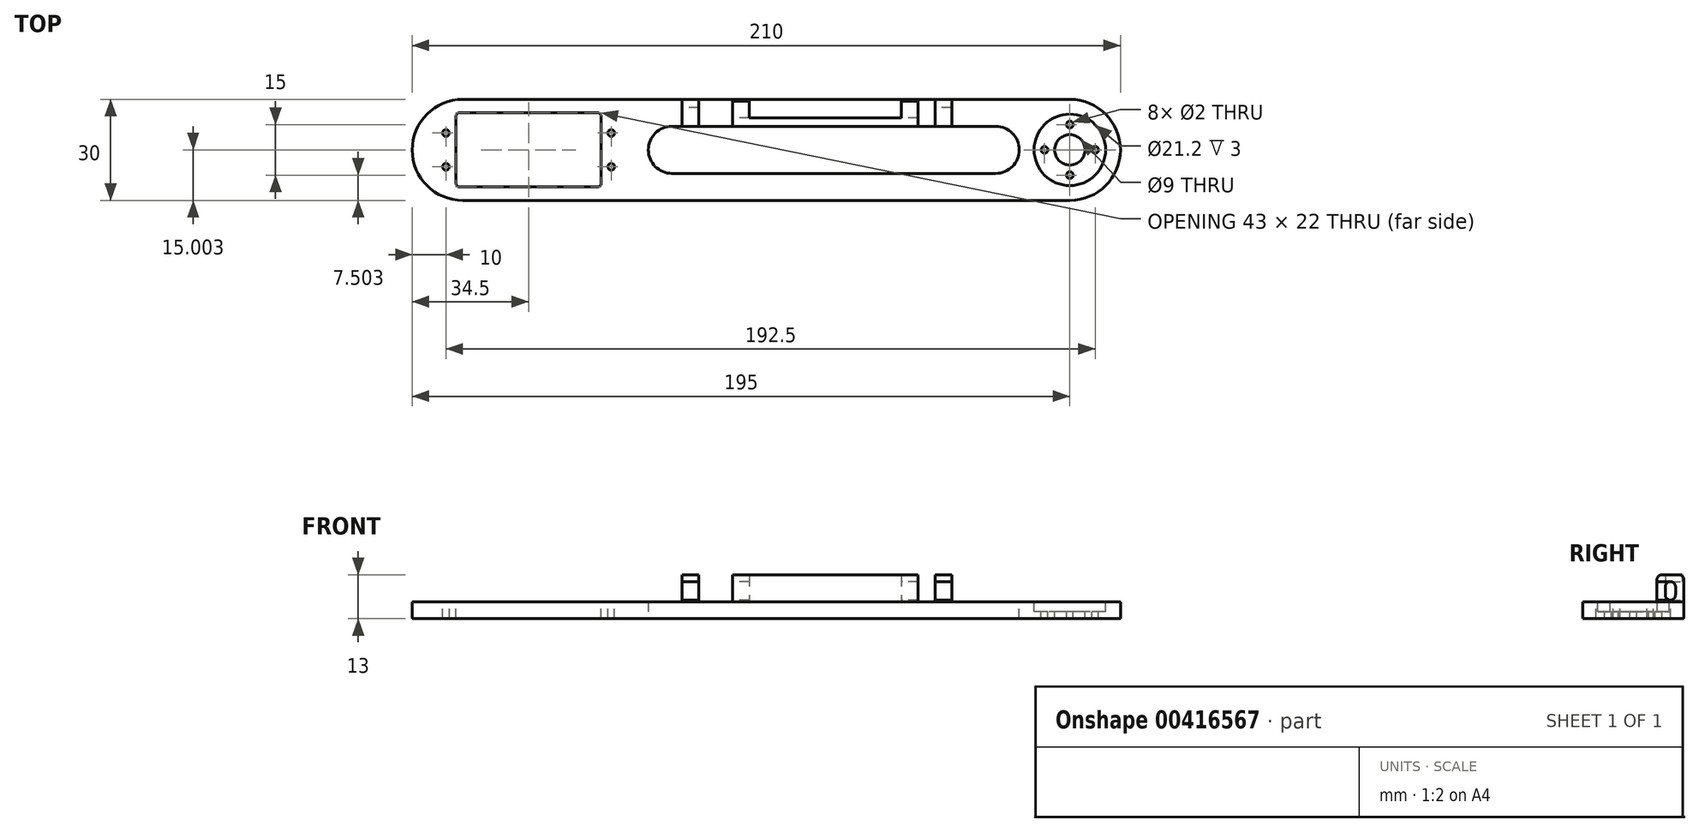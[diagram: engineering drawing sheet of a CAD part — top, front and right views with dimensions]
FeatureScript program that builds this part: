
annotation { "Feature Type Name" : "Feature", "Feature Type Description" : "" }
export const myFeature = defineFeature(function(context is Context, id is Id, definition is map)
    precondition{}
    {
        {
            var Q0;
            Q0=qCreatedBy(makeId("Top.planeOp"),FACE);
            var sketch = newSketch(context, id + "F0", { "sketchPlane" : qUnion([Q0])});
            skLineSegment(sketch, "E0.bottom", {"start": v(-110, 3.1) * mm, "end": v(100, 3.1) * mm});
            skLineSegment(sketch, "E0.top", {"start": v(-110, -26.9) * mm, "end": v(100, -26.9) * mm});
            skLineSegment(sketch, "E0.left", {"start": v(-110, 3.1) * mm, "end": v(-110, -26.9) * mm});
            skLineSegment(sketch, "E0.right", {"start": v(100, 3.1) * mm, "end": v(100, -26.9) * mm});
            skLineSegment(sketch, "E1.bottom", {"start": v(-40, -4.9) * mm, "end": v(70, -4.9) * mm});
            skLineSegment(sketch, "E1.top", {"start": v(-40, -18.9) * mm, "end": v(70, -18.9) * mm});
            skLineSegment(sketch, "E1.left", {"start": v(-40, -4.9) * mm, "end": v(-40, -18.9) * mm});
            skLineSegment(sketch, "E1.right", {"start": v(70, -4.9) * mm, "end": v(70, -18.9) * mm});
            skSolve(sketch);
        }
        {
            var Q0;
            Q0=makeQuery(id+"F0.imprint","IMPRINT",FACE,{"disambiguationData":[TD([[makeQuery(id+"F0.imprint","IMPRINT",EDGE,{"derivedFrom":sQuery(id+"F0.wireOp",EDGE,"E0.bottom")}),-1.0]])]});
            extrude(context, id + "F1", {"entities" : qUnion([Q0]), "depth" : 5 * mm});
        }
        {
            var Q0;
            Q0=makeQuery(id+"F1.opExtrude","CAP_FACE",FACE,{"disambiguationData":[OSD([sQuery(id+"F0.wireOp",EDGE,"E0.bottom"),sQuery(id+"F0.wireOp",EDGE,"E0.top"),sQuery(id+"F0.wireOp",EDGE,"E0.left"),sQuery(id+"F0.wireOp",EDGE,"E0.right")])],"isStart":false});
            var sketch = newSketch(context, id + "F2", { "sketchPlane" : qUnion([Q0])});
            skCircle(sketch, "E2", {"center": v(85, -11.9) * mm, "radius": 10.6 * mm});
            skCircle(sketch, "E3", {"center": v(85, -11.9) * mm, "radius": 4.5 * mm});
            skCircle(sketch, "E4", {"center": v(85, -4.4) * mm, "radius": 1 * mm});
            skCircle(sketch, "E5", {"center": v(85, -19.4) * mm, "radius": 1 * mm});
            skCircle(sketch, "E6", {"center": v(92.5, -11.9) * mm, "radius": 1 * mm});
            skCircle(sketch, "E7", {"center": v(77.5, -11.9) * mm, "radius": 1 * mm});
            skCircle(sketch, "E8", {"center": v(-65, -11.9) * mm, "radius": 2.75 * mm});
            skLineSegment(sketch, "E9.bottom", {"start": v(-97, -0.9) * mm, "end": v(-54, -0.9) * mm});
            skLineSegment(sketch, "E9.top", {"start": v(-97, -22.9) * mm, "end": v(-54, -22.9) * mm});
            skLineSegment(sketch, "E9.left", {"start": v(-97, -0.9) * mm, "end": v(-97, -22.9) * mm});
            skLineSegment(sketch, "E9.right", {"start": v(-54, -0.9) * mm, "end": v(-54, -22.9) * mm});
            skCircle(sketch, "E10", {"center": v(-51, -6.9) * mm, "radius": 1 * mm});
            skCircle(sketch, "E11", {"center": v(-51, -16.9) * mm, "radius": 1 * mm});
            skCircle(sketch, "E12", {"center": v(-100, -6.9) * mm, "radius": 1 * mm});
            skCircle(sketch, "E13", {"center": v(-100, -16.9) * mm, "radius": 1 * mm});
            skSolve(sketch);
        }
        {
            var Q0;
            Q0=makeQuery(id+"F2.imprint","IMPRINT",FACE,{"disambiguationData":[TD([[makeQuery(id+"F2.imprint","IMPRINT",EDGE,{"derivedFrom":sQuery(id+"F2.wireOp",EDGE,"E2")}),1.0]])]});
            var Q1;
            Q1=makeQuery(id+"F2.imprint","IMPRINT",FACE,{"disambiguationData":[TD([[makeQuery(id+"F2.imprint","IMPRINT",EDGE,{"derivedFrom":sQuery(id+"F2.wireOp",EDGE,"E8")}),-1.0]])]});
            extrude(context, id + "F3", {"entities" : qUnion([Q0, Q1]), "operationType" : NewBodyOperationType.REMOVE, "oppositeDirection" : true, "depth" : 3 * mm});
        }
        {
            var Q0;
            Q0=makeQuery(id+"F2.imprint","IMPRINT",FACE,{"disambiguationData":[TD([[makeQuery(id+"F2.imprint","IMPRINT",EDGE,{"derivedFrom":sQuery(id+"F2.wireOp",EDGE,"E3")}),1.0]])]});
            var Q1;
            Q1=makeQuery(id+"F2.imprint","IMPRINT",FACE,{"disambiguationData":[TD([[makeQuery(id+"F2.imprint","IMPRINT",EDGE,{"derivedFrom":sQuery(id+"F2.wireOp",EDGE,"E4")}),1.0]])]});
            var Q2;
            Q2=makeQuery(id+"F2.imprint","IMPRINT",FACE,{"disambiguationData":[TD([[makeQuery(id+"F2.imprint","IMPRINT",EDGE,{"derivedFrom":sQuery(id+"F2.wireOp",EDGE,"E7")}),1.0]])]});
            var Q3;
            Q3=makeQuery(id+"F2.imprint","IMPRINT",FACE,{"disambiguationData":[TD([[makeQuery(id+"F2.imprint","IMPRINT",EDGE,{"derivedFrom":sQuery(id+"F2.wireOp",EDGE,"E5")}),1.0]])]});
            var Q4;
            Q4=makeQuery(id+"F2.imprint","IMPRINT",FACE,{"disambiguationData":[TD([[makeQuery(id+"F2.imprint","IMPRINT",EDGE,{"derivedFrom":sQuery(id+"F2.wireOp",EDGE,"E6")}),1.0]])]});
            var Q5;
            Q5=makeQuery(id+"F2.imprint","IMPRINT",FACE,{"disambiguationData":[TD([[makeQuery(id+"F2.imprint","IMPRINT",EDGE,{"derivedFrom":sQuery(id+"F2.wireOp",EDGE,"E8")}),1.0]])]});
            var Q6;
            Q6=makeQuery(id+"F2.imprint","IMPRINT",FACE,{"disambiguationData":[TD([[makeQuery(id+"F2.imprint","IMPRINT",EDGE,{"derivedFrom":sQuery(id+"F2.wireOp",EDGE,"BxBnCqye-svmn-VfxW-Yds5-lMc6FiJJZGoG")}),1.0]])]});
            var Q7;
            Q7=makeQuery(id+"F2.imprint","IMPRINT",FACE,{"disambiguationData":[TD([[makeQuery(id+"F2.imprint","IMPRINT",EDGE,{"derivedFrom":sQuery(id+"F2.wireOp",EDGE,"Fvn0a9T8-UYAr-KfxW-xJAN-rbL94ZbWyBAD")}),1.0]])]});
            var Q8;
            Q8=makeQuery(id+"F2.imprint","IMPRINT",FACE,{"disambiguationData":[TD([[makeQuery(id+"F2.imprint","IMPRINT",EDGE,{"derivedFrom":sQuery(id+"F2.wireOp",EDGE,"IbQh5voC-LfIl-WeLM-aWEU-xkcyqfmnFLrg")}),1.0]])]});
            var Q9;
            Q9=makeQuery(id+"F2.imprint","IMPRINT",FACE,{"disambiguationData":[TD([[makeQuery(id+"F2.imprint","IMPRINT",EDGE,{"derivedFrom":sQuery(id+"F2.wireOp",EDGE,"Jml5Gy1f-vHH9-9BCY-gYTi-q249JlMg9aTh")}),1.0]])]});
            var Q10;
            Q10=makeQuery(id+"F2.imprint","IMPRINT",FACE,{"disambiguationData":[TD([[makeQuery(id+"F2.imprint","IMPRINT",EDGE,{"derivedFrom":sQuery(id+"F2.wireOp",EDGE,"E8")}),-1.0]])]});
            var Q11;
            Q11=makeQuery(id+"F2.imprint","IMPRINT",FACE,{"disambiguationData":[TD([[makeQuery(id+"F2.imprint","IMPRINT",EDGE,{"derivedFrom":sQuery(id+"F2.wireOp",EDGE,"PWfKf39f-ZtnN-yRcJ-nhmC-XpGRIvCBta7a")}),1.0]])]});
            var Q12;
            Q12=makeQuery(id+"F2.imprint","IMPRINT",FACE,{"disambiguationData":[TD([[makeQuery(id+"F2.imprint","IMPRINT",EDGE,{"derivedFrom":sQuery(id+"F2.wireOp",EDGE,"gZUGkUCZ-vtm3-Om3j-GvZn-Frgqdlfowhft")}),1.0]])]});
            extrude(context, id + "F4", {"entities" : qUnion([Q0, Q1, Q2, Q3, Q4, Q5, Q6, Q7, Q8, Q9, Q10, Q11, Q12]), "operationType" : NewBodyOperationType.REMOVE, "oppositeDirection" : true, "depth" : 25 * mm});
        }
        {
            var Q0;
            Q0=makeQuery(id+"F1.opExtrude","SWEPT_EDGE",EDGE,{"disambiguationData":[OSD([sQuery(id+"F0.wireOp",EDGE,"E0.bottom"),sQuery(id+"F0.wireOp",EDGE,"E0.right")])]});
            var Q1;
            Q1=makeQuery(id+"F1.opExtrude","SWEPT_EDGE",EDGE,{"disambiguationData":[OSD([sQuery(id+"F0.wireOp",EDGE,"E0.top"),sQuery(id+"F0.wireOp",EDGE,"E0.right")])]});
            var Q2;
            Q2=makeQuery(id+"F1.opExtrude","SWEPT_EDGE",EDGE,{"disambiguationData":[OSD([sQuery(id+"F0.wireOp",EDGE,"E0.top"),sQuery(id+"F0.wireOp",EDGE,"E0.left")])]});
            var Q3;
            Q3=makeQuery(id+"F1.opExtrude","SWEPT_EDGE",EDGE,{"disambiguationData":[OSD([sQuery(id+"F0.wireOp",EDGE,"E0.bottom"),sQuery(id+"F0.wireOp",EDGE,"E0.left")])]});
            fillet(context, id + "F5", {"entities" : qUnion([Q0, Q1, Q2, Q3]), "radius" : 15 * mm, "tangentPropagation" : true, "allowEdgeOverflow" : false});
        }
        {
            var Q0;
            Q0=makeQuery(id+"F1.opExtrude","SWEPT_EDGE",EDGE,{"disambiguationData":[OSD([sQuery(id+"F0.wireOp",EDGE,"E1.bottom"),sQuery(id+"F0.wireOp",EDGE,"E1.left")])]});
            var Q1;
            Q1=makeQuery(id+"F1.opExtrude","SWEPT_EDGE",EDGE,{"disambiguationData":[OSD([sQuery(id+"F0.wireOp",EDGE,"E1.top"),sQuery(id+"F0.wireOp",EDGE,"E1.left")])]});
            var Q2;
            Q2=makeQuery(id+"F1.opExtrude","SWEPT_EDGE",EDGE,{"disambiguationData":[OSD([sQuery(id+"F0.wireOp",EDGE,"E1.bottom"),sQuery(id+"F0.wireOp",EDGE,"E1.right")])]});
            var Q3;
            Q3=makeQuery(id+"F1.opExtrude","SWEPT_EDGE",EDGE,{"disambiguationData":[OSD([sQuery(id+"F0.wireOp",EDGE,"E1.top"),sQuery(id+"F0.wireOp",EDGE,"E1.right")])]});
            fillet(context, id + "F6", {"entities" : qUnion([Q0, Q1, Q2, Q3]), "radius" : 7 * mm, "tangentPropagation" : true, "allowEdgeOverflow" : false});
        }
        {
            var Q0;
            {var subQ0=sQuery(id+"F2.wireOp",EDGE,"E9.left");var subQ1=sQuery(id+"F2.wireOp",EDGE,"E9.bottom");Q0=makeQuery(id+"F4.boolean.opBoolean","MERGE",EDGE,{"derivedFrom":[makeQuery(id+"F3.boolean.opBoolean","COPY",EDGE,{"derivedFrom":makeQuery(id+"F3.opExtrude","SWEPT_EDGE",EDGE,{"disambiguationData":[OSD([subQ1,subQ0])]})}),makeQuery(id+"F4.opExtrude","SWEPT_EDGE",EDGE,{"disambiguationData":[OSD([subQ1,subQ0])]})]});}
            var Q1;
            {var subQ0=sQuery(id+"F2.wireOp",EDGE,"E9.left");var subQ1=sQuery(id+"F2.wireOp",EDGE,"E9.top");Q1=makeQuery(id+"F4.boolean.opBoolean","MERGE",EDGE,{"derivedFrom":[makeQuery(id+"F3.boolean.opBoolean","COPY",EDGE,{"derivedFrom":makeQuery(id+"F3.opExtrude","SWEPT_EDGE",EDGE,{"disambiguationData":[OSD([subQ1,subQ0])]})}),makeQuery(id+"F4.opExtrude","SWEPT_EDGE",EDGE,{"disambiguationData":[OSD([subQ1,subQ0])]})]});}
            var Q2;
            {var subQ0=sQuery(id+"F2.wireOp",EDGE,"E9.right");var subQ1=sQuery(id+"F2.wireOp",EDGE,"E9.bottom");Q2=makeQuery(id+"F4.boolean.opBoolean","MERGE",EDGE,{"derivedFrom":[makeQuery(id+"F3.boolean.opBoolean","COPY",EDGE,{"derivedFrom":makeQuery(id+"F3.opExtrude","SWEPT_EDGE",EDGE,{"disambiguationData":[OSD([subQ1,subQ0])]})}),makeQuery(id+"F4.opExtrude","SWEPT_EDGE",EDGE,{"disambiguationData":[OSD([subQ1,subQ0])]})]});}
            var Q3;
            {var subQ0=sQuery(id+"F2.wireOp",EDGE,"E9.right");var subQ1=sQuery(id+"F2.wireOp",EDGE,"E9.top");Q3=makeQuery(id+"F4.boolean.opBoolean","MERGE",EDGE,{"derivedFrom":[makeQuery(id+"F3.boolean.opBoolean","COPY",EDGE,{"derivedFrom":makeQuery(id+"F3.opExtrude","SWEPT_EDGE",EDGE,{"disambiguationData":[OSD([subQ1,subQ0])]})}),makeQuery(id+"F4.opExtrude","SWEPT_EDGE",EDGE,{"disambiguationData":[OSD([subQ1,subQ0])]})]});}
            fillet(context, id + "F7", {"entities" : qUnion([Q0, Q1, Q2, Q3]), "radius" : 1 * mm, "tangentPropagation" : true, "allowEdgeOverflow" : false});
        }
        {
            var Q0;
            Q0=makeQuery(id+"F2.imprint","IMPRINT",FACE,{"disambiguationData":[TD([[makeQuery(id+"F2.imprint","IMPRINT",EDGE,{"derivedFrom":sQuery(id+"F2.wireOp",EDGE,"E12")}),1.0]])]});
            var Q1;
            Q1=makeQuery(id+"F2.imprint","IMPRINT",FACE,{"disambiguationData":[TD([[makeQuery(id+"F2.imprint","IMPRINT",EDGE,{"derivedFrom":sQuery(id+"F2.wireOp",EDGE,"E13")}),1.0]])]});
            var Q2;
            Q2=makeQuery(id+"F2.imprint","IMPRINT",FACE,{"disambiguationData":[TD([[makeQuery(id+"F2.imprint","IMPRINT",EDGE,{"derivedFrom":sQuery(id+"F2.wireOp",EDGE,"E10")}),1.0]])]});
            var Q3;
            Q3=makeQuery(id+"F2.imprint","IMPRINT",FACE,{"disambiguationData":[TD([[makeQuery(id+"F2.imprint","IMPRINT",EDGE,{"derivedFrom":sQuery(id+"F2.wireOp",EDGE,"E11")}),1.0]])]});
            extrude(context, id + "F8", {"entities" : qUnion([Q0, Q1, Q2, Q3]), "operationType" : NewBodyOperationType.REMOVE, "oppositeDirection" : true, "depth" : 25 * mm, "offsetDistance" : 25 * mm});
        }
        {
            var Q0;
            Q0=makeQuery(id+"F2.imprint","IMPRINT",FACE,{"disambiguationData":[TD([[makeQuery(id+"F2.imprint","IMPRINT",EDGE,{"derivedFrom":sQuery(id+"F2.wireOp",EDGE,"E2")}),-1.0]])]});
            var sketch = newSketch(context, id + "F9", { "sketchPlane" : qUnion([Q0])});
            skLineSegment(sketch, "E14.bottom", {"start": v(-30, 3.1) * mm, "end": v(-25, 3.1) * mm});
            skLineSegment(sketch, "E14.top", {"start": v(-30, -4.9) * mm, "end": v(-25, -4.9) * mm});
            skLineSegment(sketch, "E14.left", {"start": v(-30, 3.1) * mm, "end": v(-30, -4.9) * mm});
            skLineSegment(sketch, "E14.right", {"start": v(-25, 3.1) * mm, "end": v(-25, -4.9) * mm});
            skLineSegment(sketch, "E15.bottom", {"start": v(-15, 3.1) * mm, "end": v(-10, 3.1) * mm});
            skLineSegment(sketch, "E15.top", {"start": v(-15, -4.9) * mm, "end": v(-10, -4.9) * mm});
            skLineSegment(sketch, "E15.left", {"start": v(-15, 3.1) * mm, "end": v(-15, -4.9) * mm});
            skLineSegment(sketch, "E15.right", {"start": v(-10, 3.1) * mm, "end": v(-10, -4.9) * mm});
            skLineSegment(sketch, "E16.bottom", {"start": v(35, 3.1) * mm, "end": v(40, 3.1) * mm});
            skLineSegment(sketch, "E16.top", {"start": v(35, -4.9) * mm, "end": v(40, -4.9) * mm});
            skLineSegment(sketch, "E16.left", {"start": v(35, 3.1) * mm, "end": v(35, -4.9) * mm});
            skLineSegment(sketch, "E16.right", {"start": v(40, 3.1) * mm, "end": v(40, -4.9) * mm});
            skLineSegment(sketch, "E17.bottom", {"start": v(45, 3.1) * mm, "end": v(50, 3.1) * mm});
            skLineSegment(sketch, "E17.top", {"start": v(45, -4.9) * mm, "end": v(50, -4.9) * mm});
            skLineSegment(sketch, "E17.left", {"start": v(45, 3.1) * mm, "end": v(45, -4.9) * mm});
            skLineSegment(sketch, "E17.right", {"start": v(50, 3.1) * mm, "end": v(50, -4.9) * mm});
            skLineSegment(sketch, "E18.bottom", {"start": v(-10, -4.9) * mm, "end": v(35, -4.9) * mm});
            skLineSegment(sketch, "E18.top", {"start": v(-10, -2.4) * mm, "end": v(35, -2.4) * mm});
            skLineSegment(sketch, "E18.left", {"start": v(-10, -4.9) * mm, "end": v(-10, -2.4) * mm});
            skLineSegment(sketch, "E18.right", {"start": v(35, -4.9) * mm, "end": v(35, -2.4) * mm});
            skSolve(sketch);
        }
        {
            var Q0;
            Q0=makeQuery(id+"F9.imprint","IMPRINT",FACE,{"disambiguationData":[TD([[makeQuery(id+"F9.imprint","IMPRINT",EDGE,{"derivedFrom":sQuery(id+"F9.wireOp",EDGE,"E14.bottom")}),-1.0]])]});
            var Q1;
            Q1=makeQuery(id+"F9.imprint","IMPRINT",FACE,{"disambiguationData":[TD([[makeQuery(id+"F9.imprint","IMPRINT",EDGE,{"derivedFrom":sQuery(id+"F9.wireOp",EDGE,"E15.bottom")}),-1.0]])]});
            var Q2;
            Q2=makeQuery(id+"F9.imprint","IMPRINT",FACE,{"disambiguationData":[TD([[makeQuery(id+"F9.imprint","IMPRINT",EDGE,{"derivedFrom":sQuery(id+"F9.wireOp",EDGE,"E16.bottom")}),-1.0]])]});
            var Q3;
            Q3=makeQuery(id+"F9.imprint","IMPRINT",FACE,{"disambiguationData":[TD([[makeQuery(id+"F9.imprint","IMPRINT",EDGE,{"derivedFrom":sQuery(id+"F9.wireOp",EDGE,"E17.bottom")}),-1.0]])]});
            extrude(context, id + "F10", {"entities" : qUnion([Q0, Q1, Q2, Q3]), "operationType" : NewBodyOperationType.ADD, "depth" : 8 * mm, "offsetDistance" : 25 * mm});
        }
        {
            var Q0;
            Q0=makeQuery(id+"F10.opExtrude","SWEPT_FACE",FACE,{"disambiguationData":[OSD([sQuery(id+"F9.wireOp",EDGE,"E14.left")])]});
            var sketch = newSketch(context, id + "F11", { "sketchPlane" : qUnion([Q0])});
            skLineSegment(sketch, "E19.bottom", {"start": v(-0.6, 11) * mm, "end": v(4.9, 11) * mm});
            skLineSegment(sketch, "E19.top", {"start": v(-0.6, 5.5) * mm, "end": v(4.9, 5.5) * mm});
            skLineSegment(sketch, "E19.left", {"start": v(-0.6, 11) * mm, "end": v(-0.6, 5.5) * mm});
            skLineSegment(sketch, "E19.right", {"start": v(4.9, 11) * mm, "end": v(4.9, 5.5) * mm});
            skSolve(sketch);
        }
        {
            var Q0;
            Q0=makeQuery(id+"F11.imprint","IMPRINT",FACE,{"disambiguationData":[TD([[makeQuery(id+"F11.imprint","IMPRINT",EDGE,{"derivedFrom":sQuery(id+"F11.wireOp",EDGE,"E19.bottom")}),-1.0]])]});
            extrude(context, id + "F12", {"entities" : qUnion([Q0]), "operationType" : NewBodyOperationType.REMOVE, "oppositeDirection" : true, "depth" : 6 * mm, "offsetDistance" : 25 * mm});
        }
        {
            var Q0;
            Q0=makeQuery(id+"F10.opExtrude","SWEPT_FACE",FACE,{"disambiguationData":[OSD([sQuery(id+"F9.wireOp",EDGE,"E15.left")])]});
            var sketch = newSketch(context, id + "F13", { "sketchPlane" : qUnion([Q0])});
            skLineSegment(sketch, "E20.bottom", {"start": v(-3.1, 11) * mm, "end": v(2.4, 11) * mm});
            skLineSegment(sketch, "E20.top", {"start": v(-3.1, 5.5) * mm, "end": v(2.4, 5.5) * mm});
            skLineSegment(sketch, "E20.left", {"start": v(-3.1, 11) * mm, "end": v(-3.1, 5.5) * mm});
            skLineSegment(sketch, "E20.right", {"start": v(2.4, 11) * mm, "end": v(2.4, 5.5) * mm});
            skSolve(sketch);
        }
        {
            var Q0;
            Q0=makeQuery(id+"F13.imprint","IMPRINT",FACE,{"disambiguationData":[TD([[makeQuery(id+"F13.imprint","IMPRINT",EDGE,{"derivedFrom":sQuery(id+"F13.wireOp",EDGE,"E20.bottom")}),-1.0]])]});
            extrude(context, id + "F14", {"entities" : qUnion([Q0]), "operationType" : NewBodyOperationType.REMOVE, "oppositeDirection" : true, "depth" : 6 * mm, "offsetDistance" : 25 * mm});
        }
        {
            var Q0;
            Q0=makeQuery(id+"F10.opExtrude","SWEPT_FACE",FACE,{"disambiguationData":[OSD([sQuery(id+"F9.wireOp",EDGE,"E16.left")])]});
            var sketch = newSketch(context, id + "F15", { "sketchPlane" : qUnion([Q0])});
            skLineSegment(sketch, "E21.bottom", {"start": v(-3.1, 11) * mm, "end": v(2.4, 11) * mm});
            skLineSegment(sketch, "E21.top", {"start": v(-3.1, 5.5) * mm, "end": v(2.4, 5.5) * mm});
            skLineSegment(sketch, "E21.left", {"start": v(-3.1, 11) * mm, "end": v(-3.1, 5.5) * mm});
            skLineSegment(sketch, "E21.right", {"start": v(2.4, 11) * mm, "end": v(2.4, 5.5) * mm});
            skSolve(sketch);
        }
        {
            var Q0;
            Q0=makeQuery(id+"F10.opExtrude","SWEPT_FACE",FACE,{"disambiguationData":[OSD([sQuery(id+"F9.wireOp",EDGE,"E17.left")])]});
            var sketch = newSketch(context, id + "F16", { "sketchPlane" : qUnion([Q0])});
            skLineSegment(sketch, "E22.bottom", {"start": v(4.9, 11) * mm, "end": v(-0.6, 11) * mm});
            skLineSegment(sketch, "E22.top", {"start": v(4.9, 5.5) * mm, "end": v(-0.6, 5.5) * mm});
            skLineSegment(sketch, "E22.left", {"start": v(4.9, 11) * mm, "end": v(4.9, 5.5) * mm});
            skLineSegment(sketch, "E22.right", {"start": v(-0.6, 11) * mm, "end": v(-0.6, 5.5) * mm});
            skSolve(sketch);
        }
        {
            var Q0;
            Q0=makeQuery(id+"F15.imprint","IMPRINT",FACE,{"disambiguationData":[TD([[makeQuery(id+"F15.imprint","IMPRINT",EDGE,{"derivedFrom":sQuery(id+"F15.wireOp",EDGE,"E21.bottom")}),-1.0]])]});
            var Q1;
            Q1=makeQuery(id+"F16.imprint","IMPRINT",FACE,{"disambiguationData":[TD([[makeQuery(id+"F16.imprint","IMPRINT",EDGE,{"derivedFrom":sQuery(id+"F16.wireOp",EDGE,"E22.bottom")}),1.0]])]});
            extrude(context, id + "F17", {"entities" : qUnion([Q0, Q1]), "operationType" : NewBodyOperationType.REMOVE, "oppositeDirection" : true, "depth" : 6 * mm, "offsetDistance" : 25 * mm});
        }
        {
            var Q0;
            Q0=makeQuery(id+"F9.imprint","IMPRINT",FACE,{"disambiguationData":[TD([[makeQuery(id+"F9.imprint","IMPRINT",EDGE,{"derivedFrom":sQuery(id+"F9.wireOp",EDGE,"IvspVwUg-y2LT-3wGW-ULcG-3461iv4c8vu4.bottom")}),-1.0]])]});
            var Q1;
            Q1=makeQuery(id+"F9.imprint","IMPRINT",FACE,{"disambiguationData":[TD([[makeQuery(id+"F9.imprint","IMPRINT",EDGE,{"derivedFrom":sQuery(id+"F9.wireOp",EDGE,"E18.bottom")}),1.0]])]});
            extrude(context, id + "F18", {"entities" : qUnion([Q0, Q1]), "operationType" : NewBodyOperationType.ADD, "depth" : 8 * mm, "offsetDistance" : 25 * mm});
        }
        {
            var Q0;
            {var subQ3=sQuery(id+"F9.wireOp",EDGE,"E16.bottom");var subQ14=sQuery(id+"F0.wireOp",EDGE,"E0.bottom");var subQ15=sQuery(id+"F9.wireOp",EDGE,"E14.left");var subQ17=sQuery(id+"F9.wireOp",EDGE,"E14.bottom");var subQ20=sQuery(id+"F9.wireOp",EDGE,"E17.bottom");Q0=makeQuery(id+"F17.boolean.opBoolean","SPLIT",FACE,{"disambiguationData":[TD([makeQuery(id+"F17.opExtrude","SWEPT_FACE",FACE,{"disambiguationData":[OSD([sQuery(id+"F15.wireOp",EDGE,"E21.bottom")])]})])],"derivedFrom":makeQuery(id+"F14.boolean.opBoolean","SPLIT",FACE,{"disambiguationData":[TD([makeQuery(id+"F10.opExtrude","SWEPT_FACE",FACE,{"disambiguationData":[OSD([subQ15])]})])],"derivedFrom":makeQuery(id+"F10.boolean.opBoolean","MERGE",FACE,{"derivedFrom":[makeQuery(id+"F1.opExtrude","SWEPT_FACE",FACE,{"disambiguationData":[OSD([subQ14])]}),makeQuery(id+"F10.opExtrude","SWEPT_FACE",FACE,{"disambiguationData":[OSD([subQ17])]}),makeQuery(id+"F10.opExtrude","SWEPT_FACE",FACE,{"disambiguationData":[OSD([sQuery(id+"F9.wireOp",EDGE,"E15.bottom")])]}),makeQuery(id+"F10.opExtrude","SWEPT_FACE",FACE,{"disambiguationData":[OSD([subQ3])]}),makeQuery(id+"F10.opExtrude","SWEPT_FACE",FACE,{"disambiguationData":[OSD([subQ20])]})]})})});}
            var Q1;
            {var subQ3=sQuery(id+"F9.wireOp",EDGE,"E15.bottom");Q1=makeQuery(id+"F14.boolean.opBoolean","SPLIT",FACE,{"disambiguationData":[TD([makeQuery(id+"F14.opExtrude","SWEPT_FACE",FACE,{"disambiguationData":[OSD([sQuery(id+"F13.wireOp",EDGE,"E20.bottom")])]})])],"derivedFrom":makeQuery(id+"F10.boolean.opBoolean","MERGE",FACE,{"derivedFrom":[makeQuery(id+"F1.opExtrude","SWEPT_FACE",FACE,{"disambiguationData":[OSD([sQuery(id+"F0.wireOp",EDGE,"E0.bottom")])]}),makeQuery(id+"F10.opExtrude","SWEPT_FACE",FACE,{"disambiguationData":[OSD([sQuery(id+"F9.wireOp",EDGE,"E14.bottom")])]}),makeQuery(id+"F10.opExtrude","SWEPT_FACE",FACE,{"disambiguationData":[OSD([subQ3])]}),makeQuery(id+"F10.opExtrude","SWEPT_FACE",FACE,{"disambiguationData":[OSD([sQuery(id+"F9.wireOp",EDGE,"E16.bottom")])]}),makeQuery(id+"F10.opExtrude","SWEPT_FACE",FACE,{"disambiguationData":[OSD([sQuery(id+"F9.wireOp",EDGE,"E17.bottom")])]})]})});}
            var Q2;
            {var subQ2=sQuery(id+"F9.wireOp",EDGE,"E17.top");var subQ9=sQuery(id+"F9.wireOp",EDGE,"E16.top");var subQ13=sQuery(id+"F0.wireOp",EDGE,"E1.bottom");var subQ20=sQuery(id+"F9.wireOp",EDGE,"E15.left");var subQ21=sQuery(id+"F9.wireOp",EDGE,"E15.top");Q2=makeQuery(id+"F17.boolean.opBoolean","SPLIT",FACE,{"disambiguationData":[TD([makeQuery(id+"F17.opExtrude","SWEPT_FACE",FACE,{"disambiguationData":[OSD([sQuery(id+"F16.wireOp",EDGE,"E22.bottom")])]})])],"derivedFrom":makeQuery(id+"F12.boolean.opBoolean","SPLIT",FACE,{"disambiguationData":[TD([makeQuery(id+"F10.opExtrude","SWEPT_FACE",FACE,{"disambiguationData":[OSD([subQ20])]})])],"derivedFrom":makeQuery(id+"F10.boolean.opBoolean","MERGE",FACE,{"derivedFrom":[makeQuery(id+"F1.opExtrude","SWEPT_FACE",FACE,{"disambiguationData":[OSD([subQ13])]}),makeQuery(id+"F10.opExtrude","SWEPT_FACE",FACE,{"disambiguationData":[OSD([sQuery(id+"F9.wireOp",EDGE,"E14.top")])]}),makeQuery(id+"F10.opExtrude","SWEPT_FACE",FACE,{"disambiguationData":[OSD([subQ21])]}),makeQuery(id+"F10.opExtrude","SWEPT_FACE",FACE,{"disambiguationData":[OSD([subQ9])]}),makeQuery(id+"F10.opExtrude","SWEPT_FACE",FACE,{"disambiguationData":[OSD([subQ2])]})]})})});}
            var Q3;
            {var subQ2=sQuery(id+"F9.wireOp",EDGE,"E14.top");Q3=makeQuery(id+"F12.boolean.opBoolean","SPLIT",FACE,{"disambiguationData":[TD([makeQuery(id+"F12.opExtrude","SWEPT_FACE",FACE,{"disambiguationData":[OSD([sQuery(id+"F11.wireOp",EDGE,"E19.bottom")])]})])],"derivedFrom":makeQuery(id+"F10.boolean.opBoolean","MERGE",FACE,{"derivedFrom":[makeQuery(id+"F1.opExtrude","SWEPT_FACE",FACE,{"disambiguationData":[OSD([sQuery(id+"F0.wireOp",EDGE,"E1.bottom")])]}),makeQuery(id+"F10.opExtrude","SWEPT_FACE",FACE,{"disambiguationData":[OSD([subQ2])]}),makeQuery(id+"F10.opExtrude","SWEPT_FACE",FACE,{"disambiguationData":[OSD([sQuery(id+"F9.wireOp",EDGE,"E15.top")])]}),makeQuery(id+"F10.opExtrude","SWEPT_FACE",FACE,{"disambiguationData":[OSD([sQuery(id+"F9.wireOp",EDGE,"E16.top")])]}),makeQuery(id+"F10.opExtrude","SWEPT_FACE",FACE,{"disambiguationData":[OSD([sQuery(id+"F9.wireOp",EDGE,"E17.top")])]})]})});}
            extrude(context, id + "F19", {"entities" : qUnion([Q0, Q1, Q2, Q3]), "operationType" : NewBodyOperationType.REMOVE, "oppositeDirection" : true, "depth" : 0.5 * mm, "offsetDistance" : 25 * mm});
        }
        {
            var Q0;
            Q0=makeQuery(id+"F10.opExtrude","CAP_EDGE",EDGE,{"disambiguationData":[OSD([sQuery(id+"F9.wireOp",EDGE,"E14.bottom")])],"isStart":false});
            var Q1;
            Q1=makeQuery(id+"F10.opExtrude","CAP_EDGE",EDGE,{"disambiguationData":[OSD([sQuery(id+"F9.wireOp",EDGE,"E14.top")])],"isStart":false});
            var Q2;
            Q2=makeQuery(id+"F10.opExtrude","CAP_EDGE",EDGE,{"disambiguationData":[OSD([sQuery(id+"F9.wireOp",EDGE,"E15.top")])],"isStart":false});
            var Q3;
            Q3=makeQuery(id+"F10.opExtrude","CAP_EDGE",EDGE,{"disambiguationData":[OSD([sQuery(id+"F9.wireOp",EDGE,"E15.bottom")])],"isStart":false});
            var Q4;
            Q4=makeQuery(id+"F14.boolean.opBoolean","COPY",EDGE,{"derivedFrom":makeQuery(id+"F14.opExtrude","SWEPT_EDGE",EDGE,{"disambiguationData":[OSD([sQuery(id+"F13.wireOp",EDGE,"E20.top"),sQuery(id+"F13.wireOp",EDGE,"E20.right")])]})});
            var Q5;
            Q5=makeQuery(id+"F14.boolean.opBoolean","COPY",EDGE,{"derivedFrom":makeQuery(id+"F14.opExtrude","SWEPT_EDGE",EDGE,{"disambiguationData":[OSD([sQuery(id+"F13.wireOp",EDGE,"E20.bottom"),sQuery(id+"F13.wireOp",EDGE,"E20.right")])]})});
            var Q6;
            Q6=makeQuery(id+"F12.boolean.opBoolean","COPY",EDGE,{"derivedFrom":makeQuery(id+"F12.opExtrude","SWEPT_EDGE",EDGE,{"disambiguationData":[OSD([sQuery(id+"F11.wireOp",EDGE,"E19.top"),sQuery(id+"F11.wireOp",EDGE,"E19.left")])]})});
            var Q7;
            Q7=makeQuery(id+"F12.boolean.opBoolean","COPY",EDGE,{"derivedFrom":makeQuery(id+"F12.opExtrude","SWEPT_EDGE",EDGE,{"disambiguationData":[OSD([sQuery(id+"F11.wireOp",EDGE,"E19.bottom"),sQuery(id+"F11.wireOp",EDGE,"E19.left")])]})});
            var Q8;
            Q8=makeQuery(id+"F10.opExtrude","CAP_EDGE",EDGE,{"disambiguationData":[OSD([sQuery(id+"F9.wireOp",EDGE,"E16.bottom")])],"isStart":false});
            var Q9;
            Q9=makeQuery(id+"F10.opExtrude","CAP_EDGE",EDGE,{"disambiguationData":[OSD([sQuery(id+"F9.wireOp",EDGE,"E17.bottom")])],"isStart":false});
            var Q10;
            Q10=makeQuery(id+"F10.opExtrude","CAP_EDGE",EDGE,{"disambiguationData":[OSD([sQuery(id+"F9.wireOp",EDGE,"E16.top")])],"isStart":false});
            var Q11;
            Q11=makeQuery(id+"F10.opExtrude","CAP_EDGE",EDGE,{"disambiguationData":[OSD([sQuery(id+"F9.wireOp",EDGE,"E17.top")])],"isStart":false});
            var Q12;
            Q12=makeQuery(id+"F17.boolean.opBoolean","COPY",EDGE,{"derivedFrom":makeQuery(id+"F17.opExtrude","SWEPT_EDGE",EDGE,{"disambiguationData":[OSD([sQuery(id+"F15.wireOp",EDGE,"E21.bottom"),sQuery(id+"F15.wireOp",EDGE,"E21.right")])]})});
            var Q13;
            Q13=makeQuery(id+"F17.boolean.opBoolean","COPY",EDGE,{"derivedFrom":makeQuery(id+"F17.opExtrude","SWEPT_EDGE",EDGE,{"disambiguationData":[OSD([sQuery(id+"F15.wireOp",EDGE,"E21.top"),sQuery(id+"F15.wireOp",EDGE,"E21.right")])]})});
            var Q14;
            Q14=makeQuery(id+"F17.boolean.opBoolean","COPY",EDGE,{"derivedFrom":makeQuery(id+"F17.opExtrude","SWEPT_EDGE",EDGE,{"disambiguationData":[OSD([sQuery(id+"F16.wireOp",EDGE,"E22.top"),sQuery(id+"F16.wireOp",EDGE,"E22.right")])]})});
            var Q15;
            Q15=makeQuery(id+"F17.boolean.opBoolean","COPY",EDGE,{"derivedFrom":makeQuery(id+"F17.opExtrude","SWEPT_EDGE",EDGE,{"disambiguationData":[OSD([sQuery(id+"F16.wireOp",EDGE,"E22.bottom"),sQuery(id+"F16.wireOp",EDGE,"E22.right")])]})});
            var Q16;
            Q16=makeQuery(id+"F19.boolean.opBoolean","COPY",EDGE,{"derivedFrom":makeQuery(id+"F19.opExtrude","CAP_EDGE",EDGE,{"disambiguationData":[OSD([sQuery(id+"F9.wireOp",EDGE,"E16.bottom")])],"isStart":false})});
            var Q17;
            Q17=makeQuery(id+"F19.boolean.opBoolean","COPY",EDGE,{"derivedFrom":makeQuery(id+"F19.opExtrude","CAP_EDGE",EDGE,{"disambiguationData":[OSD([sQuery(id+"F9.wireOp",EDGE,"E15.bottom")])],"isStart":false})});
            fillet(context, id + "F20", {"entities" : qUnion([Q0, Q1, Q2, Q3, Q4, Q5, Q6, Q7, Q8, Q9, Q10, Q11, Q12, Q13, Q14, Q15, Q16, Q17]), "radius" : 1.5 * mm, "tangentPropagation" : true, "allowEdgeOverflow" : false});
        }
    });
